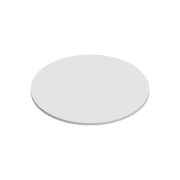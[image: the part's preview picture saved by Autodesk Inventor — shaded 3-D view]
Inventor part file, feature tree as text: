
AUTODESK INVENTOR PART (.ipt)
format: ipt  version: 2022 (Build 260153000, 153)  size: 78,336 bytes
history: native  units: mm
features: extrude x1, sketch x1
ambient origin geometry x8: Origin, YZ Plane, XZ Plane, XY Plane, X Axis, Y Axis, Z Axis, Center Point
bodies: Solid1 (feature_tree)
feature tree (2):
  extrude  "Extrusion1"  Depth=10.0mm TaperAngle=0.0deg
  sketch  "Sketch1"  dims[d0=406.6mm d1=10.0mm d2=0.0mm]
